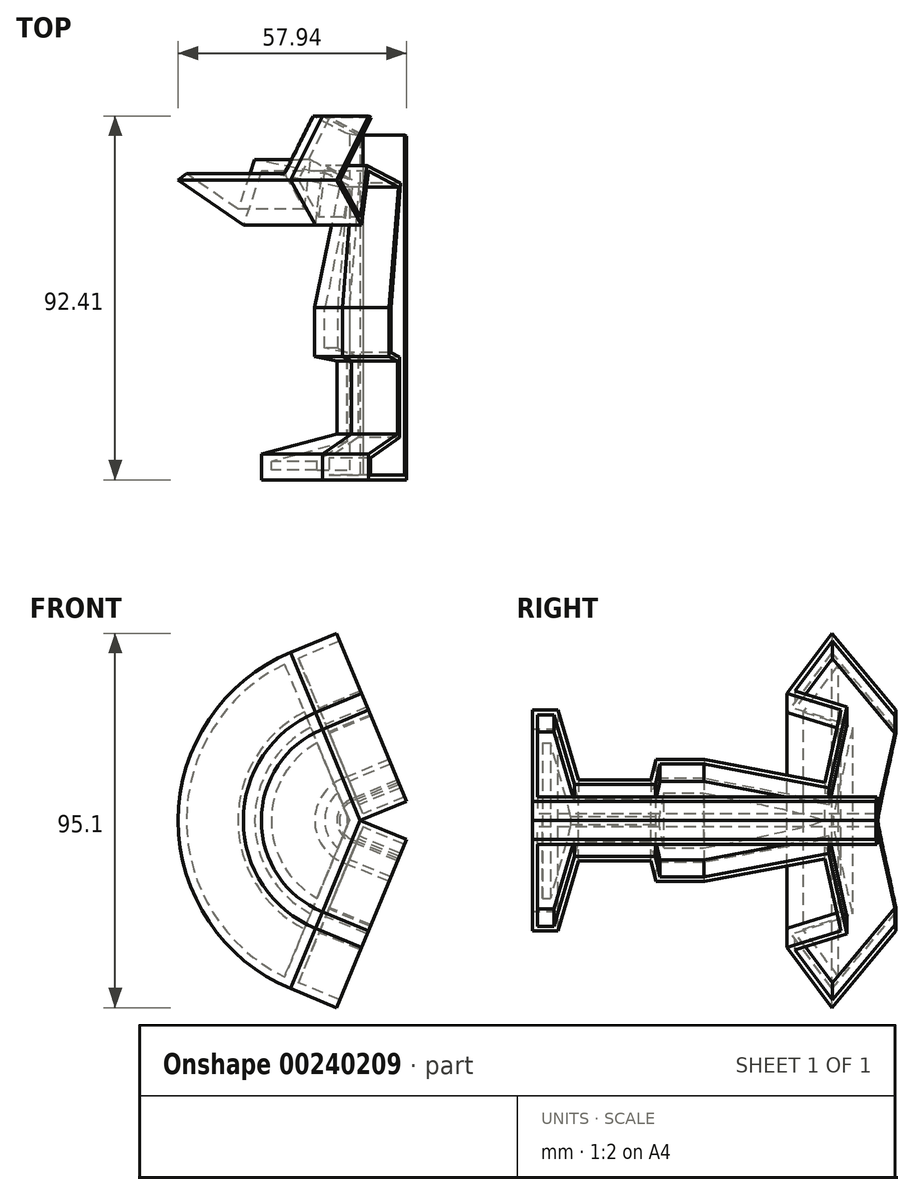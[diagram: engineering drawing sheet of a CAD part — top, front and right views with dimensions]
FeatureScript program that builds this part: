
annotation { "Feature Type Name" : "Feature", "Feature Type Description" : "" }
export const myFeature = defineFeature(function(context is Context, id is Id, definition is map)
    precondition{}
    {
        {
            var Q0;
            Q0=qCreatedBy(makeId("Top.planeOp"),FACE);
            var sketch = newSketch(context, id + "F0", { "sketchPlane" : qUnion([Q0])});
            skLineSegment(sketch, "E0", {"start": v(0, 68.32) * mm, "end": v(0, -51.2) * mm});
            skLineSegment(sketch, "E1", {"start": v(0, 43.5) * mm, "end": v(-25.1, 48.63) * mm});
            skLineSegment(sketch, "E2", {"start": v(-25.1, 48.63) * mm, "end": v(-46.2, 32.37) * mm});
            skLineSegment(sketch, "E3", {"start": v(-46.2, 32.37) * mm, "end": v(-29.67, 20.97) * mm});
            skLineSegment(sketch, "E4", {"start": v(-29.67, 20.97) * mm, "end": v(-25.1, 34.66) * mm});
            skLineSegment(sketch, "E5", {"start": v(-25.1, 34.66) * mm, "end": v(-5.26, 30.6) * mm});
            skLineSegment(sketch, "E6", {"start": v(-5.26, 30.6) * mm, "end": v(-11.52, 0) * mm});
            skLineSegment(sketch, "E7", {"start": v(-11.52, 0) * mm, "end": v(-11.52, -12.4) * mm});
            skLineSegment(sketch, "E8", {"start": v(-11.52, -12.4) * mm, "end": v(-5.87, -13.56) * mm});
            skLineSegment(sketch, "E9", {"start": v(-5.87, -13.56) * mm, "end": v(-5.87, -32.09) * mm});
            skLineSegment(sketch, "E10", {"start": v(-5.87, -32.09) * mm, "end": v(-25.1, -37.22) * mm});
            skLineSegment(sketch, "E11", {"start": v(-25.1, -37.22) * mm, "end": v(-25.1, -43.78) * mm});
            skLineSegment(sketch, "E12", {"start": v(-25.1, -43.78) * mm, "end": v(0, -43.78) * mm});
            skSolve(sketch);
        }
        {
            var Q0;
            {var subQ0=sQuery(id+"F0.wireOp",EDGE,"E1");Q0=makeQuery(id+"F0.imprint","IMPRINT",FACE,{"disambiguationData":[TD([[makeQuery(id+"F0.imprint","IMPRINT",EDGE,{"derivedFrom":subQ0}),1.0]])]});}
            var Q1;
            Q1=sQuery(id+"F0.wireOp",EDGE,"E0");
            revolve(context, id + "F1", {"entities" : qUnion([Q0]), "axis" : qUnion([Q1]), "revolveType" : RevolveType.SYMMETRIC, "angle" : 135 * degree});
        }
        {
            var Q0;
            Q0=makeQuery(id+"F1.opRevolve","CAP_FACE",FACE,{"disambiguationData":[OSD([sQuery(id+"F0.wireOp",EDGE,"E0"),sQuery(id+"F0.wireOp",EDGE,"E1"),sQuery(id+"F0.wireOp",EDGE,"E2"),sQuery(id+"F0.wireOp",EDGE,"E3"),sQuery(id+"F0.wireOp",EDGE,"E4"),sQuery(id+"F0.wireOp",EDGE,"E5"),sQuery(id+"F0.wireOp",EDGE,"E6"),sQuery(id+"F0.wireOp",EDGE,"E7"),sQuery(id+"F0.wireOp",EDGE,"E8"),sQuery(id+"F0.wireOp",EDGE,"E9"),sQuery(id+"F0.wireOp",EDGE,"E10"),sQuery(id+"F0.wireOp",EDGE,"E11"),sQuery(id+"F0.wireOp",EDGE,"E12")])],"isStart":false});
            extrude(context, id + "F2", {"entities" : qUnion([Q0]), "depth" : 12.7 * mm});
        }
        {
            var Q0;
            Q0=makeQuery(id+"F1.opRevolve","CAP_FACE",FACE,{"disambiguationData":[OSD([sQuery(id+"F0.wireOp",EDGE,"E0"),sQuery(id+"F0.wireOp",EDGE,"E1"),sQuery(id+"F0.wireOp",EDGE,"E2"),sQuery(id+"F0.wireOp",EDGE,"E3"),sQuery(id+"F0.wireOp",EDGE,"E4"),sQuery(id+"F0.wireOp",EDGE,"E5"),sQuery(id+"F0.wireOp",EDGE,"E6"),sQuery(id+"F0.wireOp",EDGE,"E7"),sQuery(id+"F0.wireOp",EDGE,"E8"),sQuery(id+"F0.wireOp",EDGE,"E9"),sQuery(id+"F0.wireOp",EDGE,"E10"),sQuery(id+"F0.wireOp",EDGE,"E11"),sQuery(id+"F0.wireOp",EDGE,"E12")])],"isStart":true});
            extrude(context, id + "F3", {"entities" : qUnion([Q0]), "depth" : 12.7 * mm});
        }
        {
            var Q0;
            Q0=makeQuery(id+"F1.opRevolve","SWEPT_FACE",FACE,{"disambiguationData":[OSD([sQuery(id+"F0.wireOp",EDGE,"E1")])]});
            var Q1;
            Q1=makeQuery(id+"F1.opRevolve","SWEPT_FACE",FACE,{"disambiguationData":[OSD([sQuery(id+"F0.wireOp",EDGE,"E2")])]});
            shell(context, id + "F4", {"entities" : qUnion([Q0, Q1]), "thickness" : 2.54 * mm});
        }
        {
            var Q0;
            Q0=makeQuery(id+"F2.opExtrude","CAP_FACE",FACE,{"disambiguationData":[OSD([sQuery(id+"F0.wireOp",EDGE,"E0"),sQuery(id+"F0.wireOp",EDGE,"E1"),sQuery(id+"F0.wireOp",EDGE,"E2"),sQuery(id+"F0.wireOp",EDGE,"E3"),sQuery(id+"F0.wireOp",EDGE,"E4"),sQuery(id+"F0.wireOp",EDGE,"E5"),sQuery(id+"F0.wireOp",EDGE,"E6"),sQuery(id+"F0.wireOp",EDGE,"E7"),sQuery(id+"F0.wireOp",EDGE,"E8"),sQuery(id+"F0.wireOp",EDGE,"E9"),sQuery(id+"F0.wireOp",EDGE,"E10"),sQuery(id+"F0.wireOp",EDGE,"E11"),sQuery(id+"F0.wireOp",EDGE,"E12")])],"isStart":false});
            var Q1;
            Q1=makeQuery(id+"F2.opExtrude","SWEPT_FACE",FACE,{"disambiguationData":[OSD([sQuery(id+"F0.wireOp",EDGE,"E1")])]});
            shell(context, id + "F5", {"entities" : qUnion([Q0, Q1]), "thickness" : 1.27 * mm});
        }
        {
            var Q0;
            Q0=makeQuery(id+"F3.opExtrude","CAP_FACE",FACE,{"disambiguationData":[OSD([sQuery(id+"F0.wireOp",EDGE,"E0"),sQuery(id+"F0.wireOp",EDGE,"E1"),sQuery(id+"F0.wireOp",EDGE,"E2"),sQuery(id+"F0.wireOp",EDGE,"E3"),sQuery(id+"F0.wireOp",EDGE,"E4"),sQuery(id+"F0.wireOp",EDGE,"E5"),sQuery(id+"F0.wireOp",EDGE,"E6"),sQuery(id+"F0.wireOp",EDGE,"E7"),sQuery(id+"F0.wireOp",EDGE,"E8"),sQuery(id+"F0.wireOp",EDGE,"E9"),sQuery(id+"F0.wireOp",EDGE,"E10"),sQuery(id+"F0.wireOp",EDGE,"E11"),sQuery(id+"F0.wireOp",EDGE,"E12")])],"isStart":false});
            var Q1;
            Q1=makeQuery(id+"F3.opExtrude","SWEPT_FACE",FACE,{"disambiguationData":[OSD([sQuery(id+"F0.wireOp",EDGE,"E1")])]});
            shell(context, id + "F6", {"entities" : qUnion([Q0, Q1]), "thickness" : 1.27 * mm});
        }
    });
